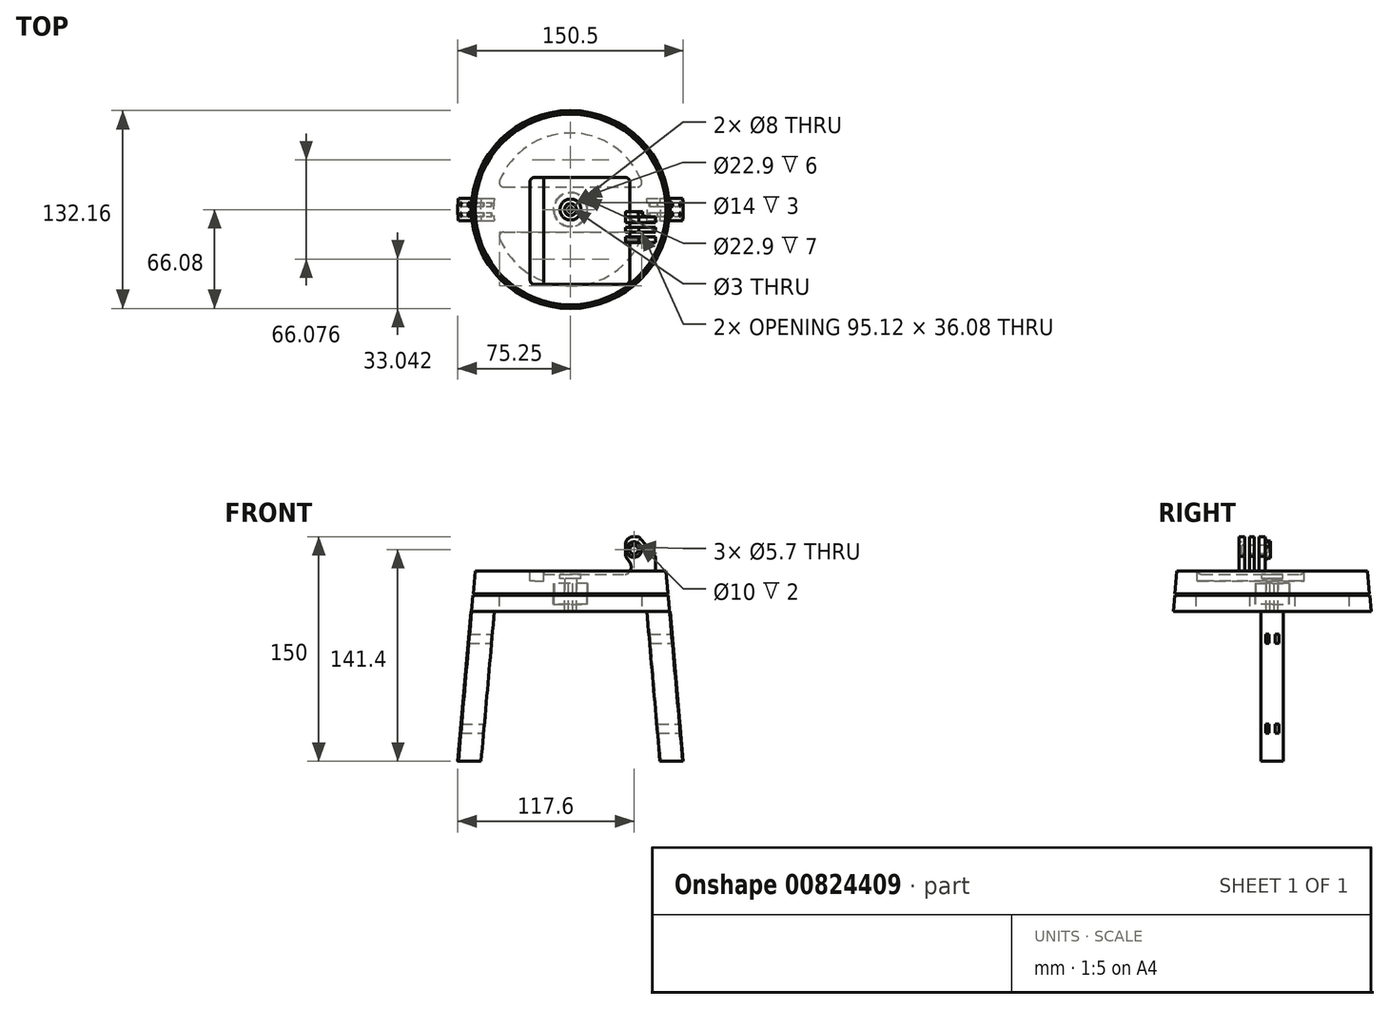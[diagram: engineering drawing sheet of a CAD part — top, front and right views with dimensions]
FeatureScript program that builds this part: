
annotation { "Feature Type Name" : "Feature", "Feature Type Description" : "" }
export const myFeature = defineFeature(function(context is Context, id is Id, definition is map)
    precondition{}
    {
        {
            var Q0;
            Q0=qCreatedBy(makeId("Top.planeOp"),FACE);
            var sketch = newSketch(context, id + "F0", { "sketchPlane" : qUnion([Q0])});
            skCircle(sketch, "E0", {"center": v(0, 0) * mm, "radius": 4 * mm});
            skCircle(sketch, "E1", {"center": v(0, 0) * mm, "radius": 11.05 * mm});
            skSolve(sketch);
        }
        {
            var Q0;
            Q0 = qSketchRegion(id + "F0", true);
            extrude(context, id + "F1", {"entities" : qUnion([Q0]), "depth" : 7 * mm, "offsetDistance" : 25 * mm});
        }
        {
            var Q0;
            Q0 = qSketchRegion(id + "F0", true);
            extrude(context, id + "F2", {"entities" : qUnion([Q0]), "oppositeDirection" : true, "depth" : 7 * mm, "offsetDistance" : 25 * mm});
        }
        {
            assignVariable(context, id + "F3", {"name" : "OuterDiameter", "anyValue" : 133});
        }
        {
            var Q0;
            Q0=qCreatedBy(makeId("Top.planeOp"),FACE);
            var sketch = newSketch(context, id + "F4", { "sketchPlane" : qUnion([Q0])});
            skCircle(sketch, "E2", {"center": v(0, 0) * mm, "radius": 11.45 * mm});
            skCircle(sketch, "E3", {"center": v(0, 0) * mm, "radius": 66.5 * mm});
            skSolve(sketch);
        }
        {
            var Q0;
            Q0 = qSketchRegion(id + "F4", true);
            extrude(context, id + "F5", {"entities" : qUnion([Q0]), "depth" : 15 * mm, "offsetDistance" : 25 * mm});
        }
        {
            var Q0;
            Q0=makeQuery(id+"F5.opExtrude","CAP_FACE",FACE,{"disambiguationData":[OSD([sQuery(id+"F4.wireOp",EDGE,"E2"),sQuery(id+"F4.wireOp",EDGE,"E3")])],"isStart":false});
            var sketch = newSketch(context, id + "F6", { "sketchPlane" : qUnion([Q0])});
            skCircle(sketch, "E4", {"center": v(0, 0) * mm, "radius": 11.45 * mm});
            skCircle(sketch, "E5", {"center": v(0, 0) * mm, "radius": 4 * mm});
            skSolve(sketch);
        }
        {
            var Q0;
            Q0 = qSketchRegion(id + "F6", true);
            var Q1;
            Q1=makeQuery(id+"F1.opExtrude","CAP_FACE",FACE,{"disambiguationData":[OSD([sQuery(id+"F0.wireOp",EDGE,"E0"),sQuery(id+"F0.wireOp",EDGE,"E1")])],"isStart":false});
            var Q2;
            Q2=makeQuery(id+"F1.opExtrude","SWEPT_BODY",BODY,{"disambiguationData":[OSD([sQuery(id+"F0.wireOp",EDGE,"E0"),sQuery(id+"F0.wireOp",EDGE,"E1")])]});
            extrude(context, id + "F7", {"entities" : qUnion([Q0]), "operationType" : NewBodyOperationType.ADD, "endBound" : BoundingType.UP_TO_SURFACE, "oppositeDirection" : true, "depth" : 4 * mm, "endBoundEntityFace" : qUnion([Q1]), "endBoundEntityBody" : qUnion([Q2]), "offsetDistance" : 25 * mm});
        }
        {
            var Q0;
            Q0=makeQuery(id+"F7.boolean.opBoolean","MERGE",FACE,{"derivedFrom":[makeQuery(id+"F5.opExtrude","CAP_FACE",FACE,{"disambiguationData":[OSD([sQuery(id+"F4.wireOp",EDGE,"E2"),sQuery(id+"F4.wireOp",EDGE,"E3")])],"isStart":false}),makeQuery(id+"F7.opExtrude","CAP_FACE",FACE,{"disambiguationData":[OSD([sQuery(id+"F6.wireOp",EDGE,"E4"),sQuery(id+"F6.wireOp",EDGE,"E5")])],"isStart":true})]});
            var sketch = newSketch(context, id + "F8", { "sketchPlane" : qUnion([Q0])});
            skCircle(sketch, "E6", {"center": v(0, 0) * mm, "radius": 7 * mm});
            skSolve(sketch);
        }
        {
            var Q0;
            Q0 = qSketchRegion(id + "F8", true);
            extrude(context, id + "F9", {"entities" : qUnion([Q0]), "operationType" : NewBodyOperationType.REMOVE, "oppositeDirection" : true, "depth" : 5 * mm, "offsetDistance" : 25 * mm});
        }
        {
            var Q0;
            Q0=qCreatedBy(makeId("Top.planeOp"),FACE);
            cPlane(context, id + "F10", {"entities" : qUnion([Q0]), "cplaneType" : CPlaneType.OFFSET, "offset" : 1 * mm, "oppositeDirection" : true, "width" : 150 * mm, "height" : 150 * mm});
        }
        {
            var Q0;
            Q0=qCreatedBy(id+"F10.planeOp",FACE);
            var sketch = newSketch(context, id + "F11", { "sketchPlane" : qUnion([Q0])});
            skCircle(sketch, "E7", {"center": v(0, 0) * mm, "radius": 66.5 * mm});
            skCircle(sketch, "E8", {"center": v(0, 0) * mm, "radius": 11.45 * mm});
            skSolve(sketch);
        }
        {
            var Q0;
            Q0 = qSketchRegion(id + "F11", true);
            extrude(context, id + "F12", {"entities" : qUnion([Q0]), "oppositeDirection" : true, "depth" : 11 * mm, "offsetDistance" : 25 * mm});
        }
        {
            var Q0;
            Q0=makeQuery(id+"F12.opExtrude","CAP_FACE",FACE,{"disambiguationData":[OSD([sQuery(id+"F11.wireOp",EDGE,"E7"),sQuery(id+"F11.wireOp",EDGE,"E8")])],"isStart":false});
            var sketch = newSketch(context, id + "F13", { "sketchPlane" : qUnion([Q0])});
            skCircle(sketch, "E9", {"center": v(0, 0) * mm, "radius": 11.45 * mm});
            skCircle(sketch, "E10", {"center": v(0, 0) * mm, "radius": 4 * mm});
            skSolve(sketch);
        }
        {
            var Q0;
            Q0 = qSketchRegion(id + "F13", true);
            extrude(context, id + "F14", {"entities" : qUnion([Q0]), "operationType" : NewBodyOperationType.ADD, "oppositeDirection" : true, "depth" : 5 * mm, "offsetDistance" : 25 * mm});
        }
        {
            var Q0;
            Q0=qCreatedBy(makeId("Front.planeOp"),FACE);
            var sketch = newSketch(context, id + "F15", { "sketchPlane" : qUnion([Q0])});
            skLineSegment(sketch, "E11", {"start": v(-66.5, -12) * mm, "end": v(-75.25, -112) * mm});
            skLineSegment(sketch, "E12", {"start": v(-75.25, -112) * mm, "end": v(-60.2, -112) * mm});
            skLineSegment(sketch, "E13", {"start": v(-60.2, -112) * mm, "end": v(-51.44, -12) * mm});
            skLineSegment(sketch, "E14", {"start": v(-66.5, -12) * mm, "end": v(-51.44, -12) * mm});
            skSolve(sketch);
        }
        {
            var Q0;
            Q0=qCreatedBy(makeId("Front.planeOp"),FACE);
            var sketch = newSketch(context, id + "F16", { "sketchPlane" : qUnion([Q0])});
            skLineSegment(sketch, "E15", {"start": v(0, 0) * mm, "end": v(0, 57.1) * mm});
            skSolve(sketch);
        }
        {
            var Q0;
            Q0 = qSketchRegion(id + "F15", true);
            var Q1;
            Q1=sQuery(id+"F16.wireOp",EDGE,"E15");
            revolve(context, id + "F17", {"surfaceOperationType" : NewSurfaceOperationType.NEW, "entities" : qUnion([Q0]), "axis" : qUnion([Q1]), "revolveType" : RevolveType.FULL});
        }
        {
            var Q0;
            Q0=qCreatedBy(makeId("Right.planeOp"),FACE);
            var sketch = newSketch(context, id + "F18", { "sketchPlane" : qUnion([Q0])});
            skLineSegment(sketch, "E16.bottom", {"start": v(7.5, -12) * mm, "end": v(96.5, -12) * mm});
            skLineSegment(sketch, "E16.top", {"start": v(7.5, -122) * mm, "end": v(96.5, -122) * mm});
            skLineSegment(sketch, "E16.left", {"start": v(7.5, -12) * mm, "end": v(7.5, -122) * mm});
            skLineSegment(sketch, "E16.right", {"start": v(96.5, -12) * mm, "end": v(96.5, -122) * mm});
            skLineSegment(sketch, "E17.MirrorCS", {"start": v(-7.5, -12) * mm, "end": v(-96.5, -12) * mm});
            skLineSegment(sketch, "E18.MirrorCS", {"start": v(-7.5, -122) * mm, "end": v(-96.5, -122) * mm});
            skLineSegment(sketch, "E19.MirrorCS", {"start": v(-96.5, -12) * mm, "end": v(-96.5, -122) * mm});
            skLineSegment(sketch, "E20.MirrorCS", {"start": v(-7.5, -12) * mm, "end": v(-7.5, -122) * mm});
            skSolve(sketch);
        }
        {
            var Q0;
            Q0 = qSketchRegion(id + "F18", true);
            extrude(context, id + "F19", {"entities" : qUnion([Q0]), "operationType" : NewBodyOperationType.REMOVE, "endBound" : BoundingType.SYMMETRIC, "oppositeDirection" : true, "depth" : (50 + getVariable(context, 'OuterDiameter')) * mm, "offsetDistance" : 25 * mm});
        }
        {
            var Q0;
            Q0=qCreatedBy(makeId("Front.planeOp"),FACE);
            var sketch = newSketch(context, id + "F20", { "sketchPlane" : qUnion([Q0])});
            skLineSegment(sketch, "E21", {"start": v(-66.08, -12) * mm, "end": v(-61.72, 37.8) * mm});
            skLineSegment(sketch, "E22", {"start": v(-66.08, -12) * mm, "end": v(-96.08, -12) * mm});
            skLineSegment(sketch, "E23", {"start": v(-96.08, -12) * mm, "end": v(-91.72, 37.8) * mm});
            skLineSegment(sketch, "E24", {"start": v(-91.72, 37.8) * mm, "end": v(-61.72, 37.8) * mm});
            skSolve(sketch);
        }
        {
            var Q0;
            Q0=qCreatedBy(makeId("Front.planeOp"),FACE);
            var sketch = newSketch(context, id + "F21", { "sketchPlane" : qUnion([Q0])});
            skLineSegment(sketch, "E25", {"start": v(0, 0) * mm, "end": v(0, 55.06) * mm});
            skSolve(sketch);
        }
        {
            var Q0;
            Q0 = qSketchRegion(id + "F20", true);
            var Q1;
            Q1=sQuery(id+"F21.wireOp",EDGE,"E25");
            revolve(context, id + "F22", {"operationType" : NewBodyOperationType.REMOVE, "surfaceOperationType" : NewSurfaceOperationType.NEW, "entities" : qUnion([Q0]), "axis" : qUnion([Q1]), "revolveType" : RevolveType.FULL, "oppositeDirection" : true});
        }
        {
            var Q0;
            Q0=makeQuery(id+"F7.boolean.opBoolean","MERGE",FACE,{"derivedFrom":[makeQuery(id+"F5.opExtrude","CAP_FACE",FACE,{"disambiguationData":[OSD([sQuery(id+"F4.wireOp",EDGE,"E2"),sQuery(id+"F4.wireOp",EDGE,"E3")])],"isStart":false}),makeQuery(id+"F7.opExtrude","CAP_FACE",FACE,{"disambiguationData":[OSD([sQuery(id+"F6.wireOp",EDGE,"E4"),sQuery(id+"F6.wireOp",EDGE,"E5")])],"isStart":true})]});
            var sketch = newSketch(context, id + "F23", { "sketchPlane" : qUnion([Q0])});
            skLineSegment(sketch, "E26", {"start": v(-24, -50) * mm, "end": v(36.5, -50) * mm});
            skLineSegment(sketch, "E27", {"start": v(-24, 21.5) * mm, "end": v(36.5, 21.5) * mm});
            skLineSegment(sketch, "E28", {"start": v(-27, 18.5) * mm, "end": v(-27, -47) * mm});
            skLineSegment(sketch, "E29", {"start": v(39.5, -47) * mm, "end": v(39.5, 18.5) * mm});
            skPoint(sketch, "E30.visualSharp", {"position": v(-27, 21.5) * mm});
            skArc(sketch, "E30.filletArc", {"start": v(-24, 21.5) * mm, "mid": v(-26.12, 20.62) * mm, "end": v(-27, 18.5) * mm});
            skPoint(sketch, "E31.visualSharp", {"position": v(39.5, 21.5) * mm});
            skArc(sketch, "E31.filletArc", {"start": v(39.5, 18.5) * mm, "mid": v(38.62, 20.62) * mm, "end": v(36.5, 21.5) * mm});
            skPoint(sketch, "E32.visualSharp", {"position": v(39.5, -50) * mm});
            skArc(sketch, "E32.filletArc", {"start": v(36.5, -50) * mm, "mid": v(38.62, -49.12) * mm, "end": v(39.5, -47) * mm});
            skPoint(sketch, "E33.visualSharp", {"position": v(-27, -50) * mm});
            skArc(sketch, "E33.filletArc", {"start": v(-27, -47) * mm, "mid": v(-26.12, -49.12) * mm, "end": v(-24, -50) * mm});
            skSolve(sketch);
        }
        {
            var Q0;
            Q0 = qSketchRegion(id + "F23", true);
            extrude(context, id + "F24", {"entities" : qUnion([Q0]), "operationType" : NewBodyOperationType.REMOVE, "oppositeDirection" : true, "depth" : 2 * mm, "offsetDistance" : 25 * mm});
        }
        {
            var Q0;
            Q0=makeQuery(id+"F24.boolean.opBoolean","COPY",FACE,{"derivedFrom":makeQuery(id+"F24.opExtrude","CAP_FACE",FACE,{"disambiguationData":[OSD([sQuery(id+"F23.wireOp",EDGE,"E26"),sQuery(id+"F23.wireOp",EDGE,"E27"),sQuery(id+"F23.wireOp",EDGE,"E28"),sQuery(id+"F23.wireOp",EDGE,"E29"),sQuery(id+"F23.wireOp",EDGE,"E30.filletArc"),sQuery(id+"F23.wireOp",EDGE,"E31.filletArc"),sQuery(id+"F23.wireOp",EDGE,"E32.filletArc"),sQuery(id+"F23.wireOp",EDGE,"E33.filletArc")])],"isStart":false})});
            var sketch = newSketch(context, id + "F25", { "sketchPlane" : qUnion([Q0])});
            skArc(sketch, "E34.0", {"start": v(-27, -47) * mm, "mid": v(-26.12, -49.12) * mm, "end": v(-24, -50) * mm});
            skLineSegment(sketch, "E34.1", {"start": v(-27, 18.5) * mm, "end": v(-27, -47) * mm});
            skArc(sketch, "E34.2", {"start": v(-24, 21.5) * mm, "mid": v(-26.12, 20.62) * mm, "end": v(-27, 18.5) * mm});
            skLineSegment(sketch, "E35", {"start": v(-24, -50) * mm, "end": v(-18, -50) * mm});
            skLineSegment(sketch, "E36", {"start": v(-18, -50) * mm, "end": v(-18, 21.5) * mm});
            skLineSegment(sketch, "E37", {"start": v(-18, 21.5) * mm, "end": v(-24, 21.5) * mm});
            skSolve(sketch);
        }
        {
            var Q0;
            Q0 = qSketchRegion(id + "F25", true);
            extrude(context, id + "F26", {"entities" : qUnion([Q0]), "operationType" : NewBodyOperationType.REMOVE, "oppositeDirection" : true, "depth" : 4.5 * mm, "offsetDistance" : 25 * mm});
        }
        {
            var Q0;
            Q0=makeQuery(id+"F24.boolean.opBoolean","COPY",EDGE,{"derivedFrom":makeQuery(id+"F24.opExtrude","CAP_EDGE",EDGE,{"disambiguationData":[OSD([sQuery(id+"F23.wireOp",EDGE,"E27")])],"isStart":false})});
            fillet(context, id + "F27", {"entities" : qUnion([Q0]), "radius" : 3 * mm, "tangentPropagation" : true, "allowEdgeOverflow" : false});
        }
        {
            var Q0;
            Q0=makeQuery(id+"F9.boolean.opBoolean","COPY",FACE,{"derivedFrom":makeQuery(id+"F9.opExtrude","CAP_FACE",FACE,{"disambiguationData":[OSD([sQuery(id+"F8.wireOp",EDGE,"E6")])],"isStart":false})});
            var sketch = newSketch(context, id + "F28", { "sketchPlane" : qUnion([Q0])});
            skCircle(sketch, "E38", {"center": v(0, 0) * mm, "radius": 3.9 * mm});
            skSolve(sketch);
        }
        {
            var Q0;
            Q0 = qSketchRegion(id + "F28", true);
            var Q1;
            Q1=makeQuery(id+"F14.boolean.opBoolean","MERGE",FACE,{"derivedFrom":[makeQuery(id+"F12.opExtrude","CAP_FACE",FACE,{"disambiguationData":[OSD([sQuery(id+"F11.wireOp",EDGE,"E7"),sQuery(id+"F11.wireOp",EDGE,"E8")])],"isStart":false}),makeQuery(id+"F14.opExtrude","CAP_FACE",FACE,{"disambiguationData":[OSD([sQuery(id+"F13.wireOp",EDGE,"E9"),sQuery(id+"F13.wireOp",EDGE,"E10")])],"isStart":true})]});
            extrude(context, id + "F29", {"entities" : qUnion([Q0]), "endBound" : BoundingType.UP_TO_SURFACE, "oppositeDirection" : true, "depth" : 16.8 * mm, "endBoundEntityFace" : qUnion([Q1]), "offsetDistance" : 25 * mm});
        }
        {
            var Q0;
            Q0=makeQuery(id+"F29.opExtrude","CAP_FACE",FACE,{"disambiguationData":[OSD([sQuery(id+"F28.wireOp",EDGE,"E38")])],"isStart":true});
            var sketch = newSketch(context, id + "F30", { "sketchPlane" : qUnion([Q0])});
            skCircle(sketch, "E39", {"center": v(0, 0) * mm, "radius": 1.5 * mm});
            skSolve(sketch);
        }
        {
            var Q0;
            Q0 = qSketchRegion(id + "F30", true);
            extrude(context, id + "F31", {"entities" : qUnion([Q0]), "operationType" : NewBodyOperationType.REMOVE, "endBound" : BoundingType.SYMMETRIC, "oppositeDirection" : true, "depth" : 72.4 * mm, "offsetDistance" : 25 * mm});
        }
        {
            var Q0;
            Q0=makeQuery(id+"F14.boolean.opBoolean","MERGE",FACE,{"derivedFrom":[makeQuery(id+"F12.opExtrude","CAP_FACE",FACE,{"disambiguationData":[OSD([sQuery(id+"F11.wireOp",EDGE,"E7"),sQuery(id+"F11.wireOp",EDGE,"E8")])],"isStart":false}),makeQuery(id+"F14.opExtrude","CAP_FACE",FACE,{"disambiguationData":[OSD([sQuery(id+"F13.wireOp",EDGE,"E9"),sQuery(id+"F13.wireOp",EDGE,"E10")])],"isStart":true})]});
            var sketch = newSketch(context, id + "F32", { "sketchPlane" : qUnion([Q0])});
            skArc(sketch, "E40", {"start": v(-47.36, -19.12) * mm, "mid": v(0, -51.08) * mm, "end": v(47.36, -19.12) * mm});
            skLineSegment(sketch, "E41", {"start": v(-44.58, 15) * mm, "end": v(44.58, 15) * mm});
            skLineSegment(sketch, "E42", {"start": v(-44.58, -15) * mm, "end": v(44.58, -15) * mm});
            skArc(sketch, "E43.trimOffspring", {"start": v(47.36, 19.12) * mm, "mid": v(0, 51.08) * mm, "end": v(-47.36, 19.12) * mm});
            skPoint(sketch, "E44.visualSharp", {"position": v(-48.82, 15) * mm});
            skArc(sketch, "E44.filletArc", {"start": v(-47.36, 19.12) * mm, "mid": v(-47.07, 16.32) * mm, "end": v(-44.58, 15) * mm});
            skPoint(sketch, "E45.visualSharp", {"position": v(48.82, 15) * mm});
            skArc(sketch, "E45.filletArc", {"start": v(44.58, 15) * mm, "mid": v(47.07, 16.32) * mm, "end": v(47.36, 19.12) * mm});
            skPoint(sketch, "E46.visualSharp", {"position": v(48.82, -15) * mm});
            skArc(sketch, "E46.filletArc", {"start": v(47.36, -19.12) * mm, "mid": v(47.07, -16.32) * mm, "end": v(44.58, -15) * mm});
            skPoint(sketch, "E47.visualSharp", {"position": v(-48.82, -15) * mm});
            skArc(sketch, "E47.filletArc", {"start": v(-44.58, -15) * mm, "mid": v(-47.07, -16.32) * mm, "end": v(-47.36, -19.12) * mm});
            skSolve(sketch);
        }
        {
            var Q0;
            Q0 = qSketchRegion(id + "F32", true);
            extrude(context, id + "F33", {"entities" : qUnion([Q0]), "operationType" : NewBodyOperationType.REMOVE, "endBound" : BoundingType.UP_TO_NEXT, "oppositeDirection" : true, "depth" : 25 * mm, "offsetDistance" : 25 * mm});
        }
        {
            var Q0;
            Q0=qCreatedBy(makeId("Right.planeOp"),FACE);
            var sketch = newSketch(context, id + "F34", { "sketchPlane" : qUnion([Q0])});
            skLineSegment(sketch, "E48.bottom", {"start": v(4.5, -27) * mm, "end": v(2, -27) * mm});
            skLineSegment(sketch, "E48.top", {"start": v(4.5, -33) * mm, "end": v(2, -33) * mm});
            skLineSegment(sketch, "E48.left", {"start": v(4.5, -27) * mm, "end": v(4.5, -33) * mm});
            skLineSegment(sketch, "E48.right", {"start": v(2, -27) * mm, "end": v(2, -33) * mm});
            skLineSegment(sketch, "E49.bottom", {"start": v(4.5, -87) * mm, "end": v(2, -87) * mm});
            skLineSegment(sketch, "E49.top", {"start": v(4.5, -93) * mm, "end": v(2, -93) * mm});
            skLineSegment(sketch, "E49.left", {"start": v(4.5, -87) * mm, "end": v(4.5, -93) * mm});
            skLineSegment(sketch, "E49.right", {"start": v(2, -87) * mm, "end": v(2, -93) * mm});
            skLineSegment(sketch, "E50.MirrorCS", {"start": v(-4.5, -33) * mm, "end": v(-2, -33) * mm});
            skLineSegment(sketch, "E51.MirrorCS", {"start": v(-4.5, -27) * mm, "end": v(-2, -27) * mm});
            skLineSegment(sketch, "E52.MirrorCS", {"start": v(-4.5, -93) * mm, "end": v(-2, -93) * mm});
            skLineSegment(sketch, "E53.MirrorCS", {"start": v(-4.5, -87) * mm, "end": v(-2, -87) * mm});
            skLineSegment(sketch, "E54.MirrorCS", {"start": v(-2, -27) * mm, "end": v(-2, -33) * mm});
            skLineSegment(sketch, "E55.MirrorCS", {"start": v(-2, -87) * mm, "end": v(-2, -93) * mm});
            skLineSegment(sketch, "E56.MirrorCS", {"start": v(-4.5, -27) * mm, "end": v(-4.5, -33) * mm});
            skLineSegment(sketch, "E57.MirrorCS", {"start": v(-4.5, -87) * mm, "end": v(-4.5, -93) * mm});
            skSolve(sketch);
        }
        {
            var Q0;
            Q0 = qSketchRegion(id + "F34", true);
            extrude(context, id + "F35", {"entities" : qUnion([Q0]), "operationType" : NewBodyOperationType.REMOVE, "endBound" : BoundingType.SYMMETRIC, "oppositeDirection" : true, "depth" : 232 * mm, "offsetDistance" : 25 * mm});
        }
        {
            var Q0;
            Q0=makeQuery(id+"F7.boolean.opBoolean","MERGE",FACE,{"derivedFrom":[makeQuery(id+"F5.opExtrude","CAP_FACE",FACE,{"disambiguationData":[OSD([sQuery(id+"F4.wireOp",EDGE,"E2"),sQuery(id+"F4.wireOp",EDGE,"E3")])],"isStart":false}),makeQuery(id+"F7.opExtrude","CAP_FACE",FACE,{"disambiguationData":[OSD([sQuery(id+"F6.wireOp",EDGE,"E4"),sQuery(id+"F6.wireOp",EDGE,"E5")])],"isStart":true})]});
            var sketch = newSketch(context, id + "F36", { "sketchPlane" : qUnion([Q0])});
            skLineSegment(sketch, "E58", {"start": v(15.9, -13.5) * mm, "end": v(84.17, -13.5) * mm});
            skLineSegment(sketch, "E59", {"start": v(36.67, -15) * mm, "end": v(56.67, -15) * mm});
            skLineSegment(sketch, "E60", {"start": v(56.67, -18.2) * mm, "end": v(36.67, -18.2) * mm});
            skLineSegment(sketch, "E61", {"start": v(36.67, -18.2) * mm, "end": v(36.67, -22.2) * mm});
            skLineSegment(sketch, "E62", {"start": v(36.67, -22.2) * mm, "end": v(56.67, -22.2) * mm});
            skLineSegment(sketch, "E63", {"start": v(36.67, -15) * mm, "end": v(36.67, -13.5) * mm});
            skLineSegment(sketch, "E64", {"start": v(56.67, -15) * mm, "end": v(56.67, -13.5) * mm});
            skLineSegment(sketch, "E65", {"start": v(56.67, -22.2) * mm, "end": v(56.67, -18.2) * mm});
            skLineSegment(sketch, "E66.MirrorCS", {"start": v(56.67, -12) * mm, "end": v(56.67, -13.5) * mm});
            skLineSegment(sketch, "E67.MirrorCS", {"start": v(36.67, -12) * mm, "end": v(36.67, -13.5) * mm});
            skLineSegment(sketch, "E68.MirrorCS", {"start": v(36.67, -12) * mm, "end": v(56.67, -12) * mm});
            skLineSegment(sketch, "E69.MirrorCS", {"start": v(36.67, -4.8) * mm, "end": v(56.67, -4.8) * mm});
            skLineSegment(sketch, "E70.MirrorCS", {"start": v(56.67, -4.8) * mm, "end": v(56.67, -8.8) * mm});
            skLineSegment(sketch, "E71.MirrorCS", {"start": v(56.67, -8.8) * mm, "end": v(36.67, -8.8) * mm});
            skLineSegment(sketch, "E72.MirrorCS", {"start": v(36.67, -8.8) * mm, "end": v(36.67, -4.8) * mm});
            skSolve(sketch);
        }
        {
            var Q0;
            Q0 = qSketchRegion(id + "F36", true);
            extrude(context, id + "F37", {"entities" : qUnion([Q0]), "operationType" : NewBodyOperationType.ADD, "depth" : 23 * mm, "offsetDistance" : 25 * mm});
        }
        {
            var Q0;
            Q0=makeQuery(id+"F37.opExtrude","SWEPT_FACE",FACE,{"disambiguationData":[OSD([sQuery(id+"F36.wireOp",EDGE,"E62")])]});
            var sketch = newSketch(context, id + "F38", { "sketchPlane" : qUnion([Q0])});
            skLineSegment(sketch, "E73", {"start": v(36.67, 25) * mm, "end": v(43.67, 15) * mm});
            skCircle(sketch, "E74", {"center": v(42.35, 29.4) * mm, "radius": 2.85 * mm});
            skLineSegment(sketch, "E75", {"start": v(36.67, 25) * mm, "end": v(36.67, 15) * mm});
            skLineSegment(sketch, "E76", {"start": v(36.67, 15) * mm, "end": v(43.67, 15) * mm});
            skLineSegment(sketch, "E77", {"start": v(45.65, 38) * mm, "end": v(56.67, 24.87) * mm});
            skLineSegment(sketch, "E78", {"start": v(56.67, 24.87) * mm, "end": v(56.67, 38) * mm});
            skLineSegment(sketch, "E79", {"start": v(56.67, 38) * mm, "end": v(45.65, 38) * mm});
            skSolve(sketch);
        }
        {
            var Q0;
            Q0 = qSketchRegion(id + "F38", true);
            var Q1;
            Q1=makeQuery(id+"F37.opExtrude","SWEPT_FACE",FACE,{"disambiguationData":[OSD([sQuery(id+"F36.wireOp",EDGE,"E69.MirrorCS")])]});
            extrude(context, id + "F39", {"entities" : qUnion([Q0]), "operationType" : NewBodyOperationType.REMOVE, "endBound" : BoundingType.UP_TO_SURFACE, "oppositeDirection" : true, "depth" : 17.7 * mm, "endBoundEntityFace" : qUnion([Q1]), "offsetDistance" : 25 * mm});
        }
        {
            var Q0;
            Q0=makeQuery(id+"F37.opExtrude","CAP_EDGE",EDGE,{"disambiguationData":[OSD([sQuery(id+"F36.wireOp",EDGE,"E61")])],"isStart":false});
            var Q1;
            {var subQ0=sQuery(id+"F36.wireOp",EDGE,"E62");var subQ1=sQuery(id+"F38.wireOp",EDGE,"E77");Q1=makeQuery(id+"F39.boolean.opBoolean","COPY",EDGE,{"disambiguationData":[topologyDisambiguationEdgeConnected([makeQuery(id+"F37.opExtrude","CAP_FACE",FACE,{"disambiguationData":[OSD([sQuery(id+"F36.wireOp",EDGE,"E60"),sQuery(id+"F36.wireOp",EDGE,"E61"),subQ0,sQuery(id+"F36.wireOp",EDGE,"E65")])],"isStart":false})])],"derivedFrom":makeQuery(id+"F39.opExtrude","SWEPT_EDGE",EDGE,{"disambiguationData":[OSD([subQ0,subQ1,sQuery(id+"F38.wireOp",EDGE,"E79")])]})});}
            var Q2;
            Q2=makeQuery(id+"F37.opExtrude","CAP_EDGE",EDGE,{"disambiguationData":[OSD([sQuery(id+"F36.wireOp",EDGE,"E63"),sQuery(id+"F36.wireOp",EDGE,"E67.MirrorCS")])],"isStart":false});
            var Q3;
            Q3=makeQuery(id+"F37.opExtrude","CAP_EDGE",EDGE,{"disambiguationData":[OSD([sQuery(id+"F36.wireOp",EDGE,"E72.MirrorCS")])],"isStart":false});
            var Q4;
            {var subQ0=sQuery(id+"F38.wireOp",EDGE,"E77");Q4=makeQuery(id+"F39.boolean.opBoolean","COPY",EDGE,{"disambiguationData":[topologyDisambiguationEdgeConnected([makeQuery(id+"F37.opExtrude","CAP_FACE",FACE,{"disambiguationData":[OSD([sQuery(id+"F36.wireOp",EDGE,"E69.MirrorCS"),sQuery(id+"F36.wireOp",EDGE,"E70.MirrorCS"),sQuery(id+"F36.wireOp",EDGE,"E71.MirrorCS"),sQuery(id+"F36.wireOp",EDGE,"E72.MirrorCS")])],"isStart":false})])],"derivedFrom":makeQuery(id+"F39.opExtrude","SWEPT_EDGE",EDGE,{"disambiguationData":[OSD([sQuery(id+"F36.wireOp",EDGE,"E62"),subQ0,sQuery(id+"F38.wireOp",EDGE,"E79")])]})});}
            var Q5;
            {var subQ0=sQuery(id+"F38.wireOp",EDGE,"E77");Q5=makeQuery(id+"F39.boolean.opBoolean","COPY",EDGE,{"disambiguationData":[topologyDisambiguationEdgeConnected([makeQuery(id+"F37.opExtrude","CAP_FACE",FACE,{"disambiguationData":[OSD([sQuery(id+"F36.wireOp",EDGE,"E59"),sQuery(id+"F36.wireOp",EDGE,"E63"),sQuery(id+"F36.wireOp",EDGE,"E64"),sQuery(id+"F36.wireOp",EDGE,"E66.MirrorCS"),sQuery(id+"F36.wireOp",EDGE,"E67.MirrorCS"),sQuery(id+"F36.wireOp",EDGE,"E68.MirrorCS")])],"isStart":false})])],"derivedFrom":makeQuery(id+"F39.opExtrude","SWEPT_EDGE",EDGE,{"disambiguationData":[OSD([sQuery(id+"F36.wireOp",EDGE,"E62"),subQ0,sQuery(id+"F38.wireOp",EDGE,"E79")])]})});}
            var Q6;
            {var subQ0=sQuery(id+"F36.wireOp",EDGE,"E61");var subQ1=sQuery(id+"F38.wireOp",EDGE,"E73");Q6=makeQuery(id+"F39.boolean.opBoolean","COPY",EDGE,{"disambiguationData":[topologyDisambiguationEdgeConnected([makeQuery(id+"F37.opExtrude","SWEPT_FACE",FACE,{"disambiguationData":[OSD([subQ0])]})])],"derivedFrom":makeQuery(id+"F39.opExtrude","SWEPT_EDGE",EDGE,{"disambiguationData":[OSD([subQ0,sQuery(id+"F36.wireOp",EDGE,"E62"),subQ1,sQuery(id+"F38.wireOp",EDGE,"E75")])]})});}
            var Q7;
            {var subQ0=sQuery(id+"F38.wireOp",EDGE,"E73");Q7=makeQuery(id+"F39.boolean.opBoolean","COPY",EDGE,{"disambiguationData":[topologyDisambiguationEdgeConnected([makeQuery(id+"F37.opExtrude","SWEPT_FACE",FACE,{"disambiguationData":[OSD([sQuery(id+"F36.wireOp",EDGE,"E63"),sQuery(id+"F36.wireOp",EDGE,"E67.MirrorCS")])]})])],"derivedFrom":makeQuery(id+"F39.opExtrude","SWEPT_EDGE",EDGE,{"disambiguationData":[OSD([sQuery(id+"F36.wireOp",EDGE,"E61"),sQuery(id+"F36.wireOp",EDGE,"E62"),subQ0,sQuery(id+"F38.wireOp",EDGE,"E75")])]})});}
            var Q8;
            {var subQ0=sQuery(id+"F38.wireOp",EDGE,"E73");Q8=makeQuery(id+"F39.boolean.opBoolean","COPY",EDGE,{"disambiguationData":[topologyDisambiguationEdgeConnected([makeQuery(id+"F37.opExtrude","SWEPT_FACE",FACE,{"disambiguationData":[OSD([sQuery(id+"F36.wireOp",EDGE,"E72.MirrorCS")])]})])],"derivedFrom":makeQuery(id+"F39.opExtrude","SWEPT_EDGE",EDGE,{"disambiguationData":[OSD([sQuery(id+"F36.wireOp",EDGE,"E61"),sQuery(id+"F36.wireOp",EDGE,"E62"),subQ0,sQuery(id+"F38.wireOp",EDGE,"E75")])]})});}
            var Q9;
            {var subQ0=sQuery(id+"F36.wireOp",EDGE,"E65");var subQ1=sQuery(id+"F38.wireOp",EDGE,"E77");Q9=makeQuery(id+"F39.boolean.opBoolean","COPY",EDGE,{"disambiguationData":[topologyDisambiguationEdgeConnected([makeQuery(id+"F37.opExtrude","SWEPT_FACE",FACE,{"disambiguationData":[OSD([subQ0])]})])],"derivedFrom":makeQuery(id+"F39.opExtrude","SWEPT_EDGE",EDGE,{"disambiguationData":[OSD([sQuery(id+"F36.wireOp",EDGE,"E62"),subQ0,subQ1,sQuery(id+"F38.wireOp",EDGE,"E78")])]})});}
            var Q10;
            {var subQ0=sQuery(id+"F38.wireOp",EDGE,"E77");Q10=makeQuery(id+"F39.boolean.opBoolean","COPY",EDGE,{"disambiguationData":[topologyDisambiguationEdgeConnected([makeQuery(id+"F37.opExtrude","SWEPT_FACE",FACE,{"disambiguationData":[OSD([sQuery(id+"F36.wireOp",EDGE,"E64"),sQuery(id+"F36.wireOp",EDGE,"E66.MirrorCS")])]})])],"derivedFrom":makeQuery(id+"F39.opExtrude","SWEPT_EDGE",EDGE,{"disambiguationData":[OSD([sQuery(id+"F36.wireOp",EDGE,"E62"),sQuery(id+"F36.wireOp",EDGE,"E65"),subQ0,sQuery(id+"F38.wireOp",EDGE,"E78")])]})});}
            var Q11;
            {var subQ0=sQuery(id+"F38.wireOp",EDGE,"E77");Q11=makeQuery(id+"F39.boolean.opBoolean","COPY",EDGE,{"disambiguationData":[topologyDisambiguationEdgeConnected([makeQuery(id+"F37.opExtrude","SWEPT_FACE",FACE,{"disambiguationData":[OSD([sQuery(id+"F36.wireOp",EDGE,"E70.MirrorCS")])]})])],"derivedFrom":makeQuery(id+"F39.opExtrude","SWEPT_EDGE",EDGE,{"disambiguationData":[OSD([sQuery(id+"F36.wireOp",EDGE,"E62"),sQuery(id+"F36.wireOp",EDGE,"E65"),subQ0,sQuery(id+"F38.wireOp",EDGE,"E78")])]})});}
            var Q12;
            {var subQ0=sQuery(id+"F36.wireOp",EDGE,"E62");var subQ1=sQuery(id+"F38.wireOp",EDGE,"E73");var subQ2=sQuery(id+"F38.wireOp",EDGE,"E76");Q12=makeQuery(id+"F39.boolean.opBoolean","COPY",EDGE,{"disambiguationData":[TD([makeQuery(id+"F37.opExtrude","SWEPT_FACE",FACE,{"disambiguationData":[OSD([sQuery(id+"F36.wireOp",EDGE,"E60")])]})])],"derivedFrom":makeQuery(id+"F39.opExtrude","SWEPT_EDGE",EDGE,{"disambiguationData":[OSD([subQ0,subQ1,subQ2])]})});}
            var Q13;
            {var subQ0=sQuery(id+"F38.wireOp",EDGE,"E73");var subQ1=sQuery(id+"F38.wireOp",EDGE,"E76");Q13=makeQuery(id+"F39.boolean.opBoolean","COPY",EDGE,{"disambiguationData":[TD([makeQuery(id+"F37.opExtrude","SWEPT_FACE",FACE,{"disambiguationData":[OSD([sQuery(id+"F36.wireOp",EDGE,"E59")])]})])],"derivedFrom":makeQuery(id+"F39.opExtrude","SWEPT_EDGE",EDGE,{"disambiguationData":[OSD([sQuery(id+"F36.wireOp",EDGE,"E62"),subQ0,subQ1])]})});}
            var Q14;
            {var subQ0=sQuery(id+"F38.wireOp",EDGE,"E73");var subQ1=sQuery(id+"F38.wireOp",EDGE,"E76");Q14=makeQuery(id+"F39.boolean.opBoolean","COPY",EDGE,{"disambiguationData":[TD([makeQuery(id+"F37.opExtrude","SWEPT_FACE",FACE,{"disambiguationData":[OSD([sQuery(id+"F36.wireOp",EDGE,"E69.MirrorCS")])]})])],"derivedFrom":makeQuery(id+"F39.opExtrude","SWEPT_EDGE",EDGE,{"disambiguationData":[OSD([sQuery(id+"F36.wireOp",EDGE,"E62"),subQ0,subQ1])]})});}
            var Q15;
            Q15=makeQuery(id+"F37.opExtrude","CAP_EDGE",EDGE,{"disambiguationData":[OSD([sQuery(id+"F36.wireOp",EDGE,"E65")])],"isStart":true});
            var Q16;
            Q16=makeQuery(id+"F37.opExtrude","CAP_EDGE",EDGE,{"disambiguationData":[OSD([sQuery(id+"F36.wireOp",EDGE,"E70.MirrorCS")])],"isStart":true});
            var Q17;
            Q17=makeQuery(id+"F37.opExtrude","CAP_EDGE",EDGE,{"disambiguationData":[OSD([sQuery(id+"F36.wireOp",EDGE,"E64"),sQuery(id+"F36.wireOp",EDGE,"E66.MirrorCS")])],"isStart":true});
            var Q18;
            {var subQ0=sQuery(id+"F36.wireOp",EDGE,"E62");Q18=makeQuery(id+"F37.boolean.opBoolean","SPLIT",EDGE,{"disambiguationData":[topologyDisambiguationEdgeConnected([makeQuery(id+"F5.opExtrude","CAP_FACE",FACE,{"disambiguationData":[OSD([sQuery(id+"F4.wireOp",EDGE,"E2"),sQuery(id+"F4.wireOp",EDGE,"E3")])],"isStart":false})])],"derivedFrom":makeQuery(id+"F37.opExtrude","CAP_EDGE",EDGE,{"disambiguationData":[OSD([subQ0])],"isStart":true})});}
            var Q19;
            {var subQ0=sQuery(id+"F36.wireOp",EDGE,"E69.MirrorCS");Q19=makeQuery(id+"F37.boolean.opBoolean","SPLIT",EDGE,{"disambiguationData":[topologyDisambiguationEdgeConnected([makeQuery(id+"F5.opExtrude","CAP_FACE",FACE,{"disambiguationData":[OSD([sQuery(id+"F4.wireOp",EDGE,"E2"),sQuery(id+"F4.wireOp",EDGE,"E3")])],"isStart":false})])],"derivedFrom":makeQuery(id+"F37.opExtrude","CAP_EDGE",EDGE,{"disambiguationData":[OSD([subQ0])],"isStart":true})});}
            fillet(context, id + "F40", {"entities" : qUnion([Q0, Q1, Q2, Q3, Q4, Q5, Q6, Q7, Q8, Q9, Q10, Q11, Q12, Q13, Q14, Q15, Q16, Q17, Q18, Q19]), "radius" : 5 * mm, "tangentPropagation" : true, "allowEdgeOverflow" : false});
        }
        {
            var Q0;
            Q0=makeQuery(id+"F37.opExtrude","SWEPT_FACE",FACE,{"disambiguationData":[OSD([sQuery(id+"F36.wireOp",EDGE,"E69.MirrorCS")])]});
            var sketch = newSketch(context, id + "F41", { "sketchPlane" : qUnion([Q0])});
            skCircle(sketch, "E80.cCircle", {"center": v(-42.35, 29.4) * mm, "radius": 4.5 * mm, "construction": true});
            skLineSegment(sketch, "E80.0", {"start": v(-44.95, 33.9) * mm, "end": v(-39.75, 33.9) * mm});
            skLineSegment(sketch, "E80.1", {"start": v(-39.75, 33.9) * mm, "end": v(-37.15, 29.4) * mm});
            skLineSegment(sketch, "E80.2", {"start": v(-37.15, 29.4) * mm, "end": v(-39.75, 24.9) * mm});
            skLineSegment(sketch, "E80.3", {"start": v(-39.75, 24.9) * mm, "end": v(-44.95, 24.9) * mm});
            skLineSegment(sketch, "E80.4", {"start": v(-44.95, 24.9) * mm, "end": v(-47.55, 29.4) * mm});
            skLineSegment(sketch, "E80.5", {"start": v(-47.55, 29.4) * mm, "end": v(-44.95, 33.9) * mm});
            skPoint(sketch, "E80.0.midPoint", {"position": v(-42.35, 33.9) * mm});
            skCircle(sketch, "E81", {"center": v(-42.35, 29.4) * mm, "radius": 5.68 * mm});
            skSolve(sketch);
        }
        {
            var Q0;
            Q0 = qSketchRegion(id + "F41", true);
            extrude(context, id + "F42", {"entities" : qUnion([Q0]), "operationType" : NewBodyOperationType.ADD, "depth" : 3.5 * mm, "offsetDistance" : 25 * mm});
        }
        {
            var Q0;
            Q0=makeQuery(id+"F42.opExtrude","CAP_EDGE",EDGE,{"disambiguationData":[OSD([sQuery(id+"F41.wireOp",EDGE,"E81")])],"isStart":true});
            fillet(context, id + "F43", {"entities" : qUnion([Q0]), "radius" : 3 * mm, "tangentPropagation" : true, "allowEdgeOverflow" : false});
        }
        {
            var Q0;
            Q0=makeQuery(id+"F37.opExtrude","SWEPT_FACE",FACE,{"disambiguationData":[OSD([sQuery(id+"F36.wireOp",EDGE,"E62")])]});
            var sketch = newSketch(context, id + "F44", { "sketchPlane" : qUnion([Q0])});
            skCircle(sketch, "E82", {"center": v(42.35, 29.4) * mm, "radius": 5 * mm});
            skSolve(sketch);
        }
        {
            var Q0;
            Q0 = qSketchRegion(id + "F44", true);
            extrude(context, id + "F45", {"entities" : qUnion([Q0]), "operationType" : NewBodyOperationType.REMOVE, "oppositeDirection" : true, "depth" : 2 * mm, "offsetDistance" : 25 * mm});
        }
    });
